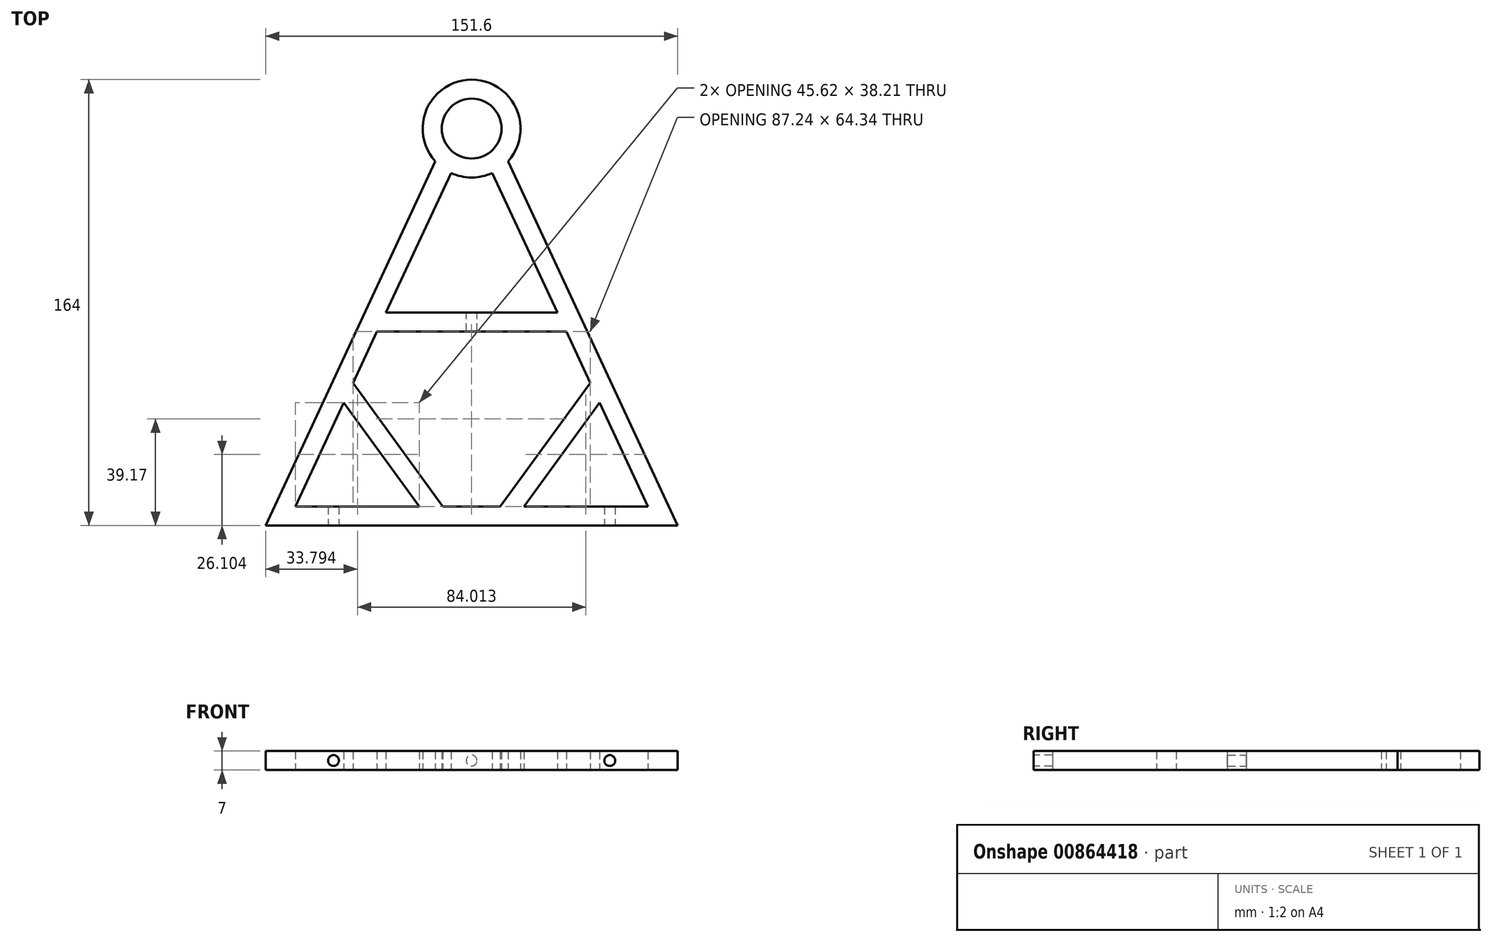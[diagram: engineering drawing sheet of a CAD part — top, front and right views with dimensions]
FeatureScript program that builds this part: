
annotation { "Feature Type Name" : "Feature", "Feature Type Description" : "" }
export const myFeature = defineFeature(function(context is Context, id is Id, definition is map)
    precondition{}
    {
        {
            var Q0;
            Q0=qCreatedBy(makeId("Top.planeOp"),FACE);
            var sketch = newSketch(context, id + "F0", { "sketchPlane" : qUnion([Q0])});
            skCircle(sketch, "E0", {"center": v(0, 0) * mm, "radius": 100 * mm, "construction": true});
            skCircle(sketch, "E1", {"center": v(0, 0) * mm, "radius": 25 * mm, "construction": true});
            skLineSegment(sketch, "E2", {"start": v(0, 0) * mm, "end": v(0, -152.48) * mm, "construction": true});
            skLineSegment(sketch, "E3", {"start": v(0, 0) * mm, "end": v(64.82, -139) * mm});
            skLineSegment(sketch, "E4", {"start": v(0, 0) * mm, "end": v(-64.82, -139) * mm});
            skCircle(sketch, "E5", {"center": v(0, 0) * mm, "radius": 11 * mm});
            skLineSegment(sketch, "E6.0", {"start": v(-6.34, 2.96) * mm, "end": v(-75.8, -146) * mm});
            skLineSegment(sketch, "E7.0", {"start": v(6.34, 2.96) * mm, "end": v(75.8, -146) * mm});
            skCircle(sketch, "E8.0", {"center": v(0, 0) * mm, "radius": 18 * mm});
            skLineSegment(sketch, "E9", {"start": v(57.36, -74.66) * mm, "end": v(0, -153.48) * mm});
            skLineSegment(sketch, "E10", {"start": v(0, -153.48) * mm, "end": v(-57.36, -74.66) * mm});
            skLineSegment(sketch, "E11", {"start": v(-57.36, -74.66) * mm, "end": v(57.36, -74.66) * mm});
            skLineSegment(sketch, "E12.0", {"start": v(71.1, -67.66) * mm, "end": v(0, -165.38) * mm});
            skLineSegment(sketch, "E12.1", {"start": v(-71.1, -67.66) * mm, "end": v(71.1, -67.66) * mm});
            skLineSegment(sketch, "E12.2", {"start": v(0, -165.38) * mm, "end": v(-71.1, -67.66) * mm});
            skLineSegment(sketch, "E13", {"start": v(-75.8, -146) * mm, "end": v(75.8, -146) * mm});
            skLineSegment(sketch, "E14.trimOffspring", {"start": v(-64.82, -139) * mm, "end": v(64.82, -139) * mm});
            skSolve(sketch);
        }
        {
            var Q0;
            {var subQ0=sQuery(id+"F0.wireOp",EDGE,"rMP4F2J8-MFNj-B9O5-1YN4-RzQH2zEwrkU1");Q0=makeQuery(id+"F0.imprint","IMPRINT",FACE,{"disambiguationData":[TD([[makeQuery(id+"F0.imprint","IMPRINT",EDGE,{"derivedFrom":subQ0}),-1.0]])]});}
            var Q1;
            {var subQ0=sQuery(id+"F0.wireOp",EDGE,"E10");Q1=makeQuery(id+"F0.imprint","IMPRINT",FACE,{"disambiguationData":[TD([[makeQuery(id+"F0.imprint","IMPRINT",EDGE,{"derivedFrom":subQ0}),1.0]])]});}
            var Q2;
            {var subQ0=sQuery(id+"F0.wireOp",EDGE,"E11");Q2=makeQuery(id+"F0.imprint","IMPRINT",FACE,{"disambiguationData":[TD([[makeQuery(id+"F0.imprint","IMPRINT",EDGE,{"derivedFrom":subQ0}),1.0]])]});}
            var Q3;
            {var subQ0=sQuery(id+"F0.wireOp",EDGE,"E9");Q3=makeQuery(id+"F0.imprint","IMPRINT",FACE,{"disambiguationData":[TD([[makeQuery(id+"F0.imprint","IMPRINT",EDGE,{"derivedFrom":subQ0}),1.0]])]});}
            var Q4;
            {var subQ8=sQuery(id+"F0.wireOp",EDGE,"1jrSBUuX-ILp1-f5az-bRsI-Kc6tBy7hKFYi");Q4=makeQuery(id+"F0.imprint","IMPRINT",FACE,{"disambiguationData":[TD([[makeQuery(id+"F0.imprint","IMPRINT",EDGE,{"derivedFrom":subQ8}),1.0]])]});}
            var Q5;
            {var subQ1=sQuery(id+"F0.wireOp",EDGE,"0f01eb31-d20b-408a-a949-16b7b9c288b3.0");var subQ5=sQuery(id+"F0.wireOp",EDGE,"E12.2");var subQ6=makeQuery(id+"F0.imprint","INTERSECT",VERTEX,{"derivedFrom":[subQ1,subQ5]});Q5=makeQuery(id+"F0.imprint","IMPRINT",FACE,{"disambiguationData":[TD([[makeQuery(id+"F0.imprint","IMPRINT",EDGE,{"disambiguationData":[TD([[subQ6,-1.0]])],"derivedFrom":subQ1}),1.0]])]});}
            var Q6;
            {var subQ1=sQuery(id+"F0.wireOp",EDGE,"E7.0");var subQ5=sQuery(id+"F0.wireOp",EDGE,"E12.1");var subQ6=makeQuery(id+"F0.imprint","INTERSECT",VERTEX,{"derivedFrom":[subQ1,subQ5]});Q6=makeQuery(id+"F0.imprint","IMPRINT",FACE,{"disambiguationData":[TD([[makeQuery(id+"F0.imprint","IMPRINT",EDGE,{"disambiguationData":[TD([[subQ6,-1.0]])],"derivedFrom":subQ1}),-1.0]])]});}
            var Q7;
            {var subQ0=sQuery(id+"F0.wireOp",EDGE,"E8.0");var subQ1=sQuery(id+"F0.wireOp",EDGE,"E3");var subQ2=makeQuery(id+"F0.imprint","INTERSECT",VERTEX,{"derivedFrom":[subQ1,subQ0]});Q7=makeQuery(id+"F0.imprint","IMPRINT",FACE,{"disambiguationData":[TD([[makeQuery(id+"F0.imprint","IMPRINT",EDGE,{"disambiguationData":[TD([[subQ2,-1.0]])],"derivedFrom":subQ1}),1.0]])]});}
            var Q8;
            {var subQ0=sQuery(id+"F0.wireOp",EDGE,"E12.1");var subQ1=sQuery(id+"F0.wireOp",EDGE,"E6.0");var subQ2=makeQuery(id+"F0.imprint","INTERSECT",VERTEX,{"derivedFrom":[subQ1,subQ0]});Q8=makeQuery(id+"F0.imprint","IMPRINT",FACE,{"disambiguationData":[TD([[makeQuery(id+"F0.imprint","IMPRINT",EDGE,{"disambiguationData":[TD([[subQ2,-1.0]])],"derivedFrom":subQ1}),1.0]])]});}
            var Q9;
            {var subQ0=sQuery(id+"F0.wireOp",EDGE,"E8.0");var subQ1=sQuery(id+"F0.wireOp",EDGE,"E4");var subQ2=makeQuery(id+"F0.imprint","INTERSECT",VERTEX,{"derivedFrom":[subQ1,subQ0]});Q9=makeQuery(id+"F0.imprint","IMPRINT",FACE,{"disambiguationData":[TD([[makeQuery(id+"F0.imprint","IMPRINT",EDGE,{"disambiguationData":[TD([[subQ2,-1.0]])],"derivedFrom":subQ1}),-1.0]])]});}
            var Q10;
            {var subQ0=sQuery(id+"F0.wireOp",EDGE,"E6.0");var subQ1=sQuery(id+"F0.wireOp",EDGE,"E5");var subQ2=makeQuery(id+"F0.imprint","INTERSECT",VERTEX,{"derivedFrom":[subQ1,subQ0]});Q10=makeQuery(id+"F0.imprint","IMPRINT",FACE,{"disambiguationData":[TD([[makeQuery(id+"F0.imprint","IMPRINT",EDGE,{"disambiguationData":[TD([[subQ2,1.0]])],"derivedFrom":subQ1}),-1.0]])]});}
            var Q11;
            {var subQ0=sQuery(id+"F0.wireOp",EDGE,"E5");var subQ1=sQuery(id+"F0.wireOp",EDGE,"E4");var subQ2=makeQuery(id+"F0.imprint","INTERSECT",VERTEX,{"derivedFrom":[subQ1,subQ0]});Q11=makeQuery(id+"F0.imprint","IMPRINT",FACE,{"disambiguationData":[TD([[makeQuery(id+"F0.imprint","IMPRINT",EDGE,{"disambiguationData":[TD([[subQ2,-1.0]])],"derivedFrom":subQ1}),-1.0]])]});}
            var Q12;
            {var subQ0=sQuery(id+"F0.wireOp",EDGE,"E5");var subQ1=sQuery(id+"F0.wireOp",EDGE,"E3");var subQ2=makeQuery(id+"F0.imprint","INTERSECT",VERTEX,{"derivedFrom":[subQ1,subQ0]});Q12=makeQuery(id+"F0.imprint","IMPRINT",FACE,{"disambiguationData":[TD([[makeQuery(id+"F0.imprint","IMPRINT",EDGE,{"disambiguationData":[TD([[subQ2,-1.0]])],"derivedFrom":subQ1}),-1.0]])]});}
            var Q13;
            {var subQ0=sQuery(id+"F0.wireOp",EDGE,"E5");var subQ1=sQuery(id+"F0.wireOp",EDGE,"E3");var subQ2=makeQuery(id+"F0.imprint","INTERSECT",VERTEX,{"derivedFrom":[subQ1,subQ0]});Q13=makeQuery(id+"F0.imprint","IMPRINT",FACE,{"disambiguationData":[TD([[makeQuery(id+"F0.imprint","IMPRINT",EDGE,{"disambiguationData":[TD([[subQ2,-1.0]])],"derivedFrom":subQ1}),1.0]])]});}
            var Q14;
            {var subQ0=sQuery(id+"F0.wireOp",EDGE,"E11");var subQ1=sQuery(id+"F0.wireOp",EDGE,"E3");var subQ2=makeQuery(id+"F0.imprint","INTERSECT",VERTEX,{"derivedFrom":[subQ1,subQ0]});Q14=makeQuery(id+"F0.imprint","IMPRINT",FACE,{"disambiguationData":[TD([[makeQuery(id+"F0.imprint","IMPRINT",EDGE,{"disambiguationData":[TD([[subQ2,-1.0]])],"derivedFrom":subQ1}),1.0]])]});}
            var Q15;
            {var subQ0=sQuery(id+"F0.wireOp",EDGE,"E11");var subQ1=sQuery(id+"F0.wireOp",EDGE,"E4");var subQ2=makeQuery(id+"F0.imprint","INTERSECT",VERTEX,{"derivedFrom":[subQ1,subQ0]});Q15=makeQuery(id+"F0.imprint","IMPRINT",FACE,{"disambiguationData":[TD([[makeQuery(id+"F0.imprint","IMPRINT",EDGE,{"disambiguationData":[TD([[subQ2,-1.0]])],"derivedFrom":subQ1}),-1.0]])]});}
            var Q16;
            {var subQ3=sQuery(id+"F0.wireOp",EDGE,"E4");var subQ7=sQuery(id+"F0.wireOp",EDGE,"E14.trimOffspring");var subQ10=makeQuery(id+"F0.imprint","INTERSECT",VERTEX,{"derivedFrom":[subQ3,subQ7]});Q16=makeQuery(id+"F0.imprint","IMPRINT",FACE,{"disambiguationData":[TD([[makeQuery(id+"F0.imprint","IMPRINT",EDGE,{"disambiguationData":[TD([[subQ10,1.0]])],"derivedFrom":subQ3}),-1.0]])]});}
            var Q17;
            {var subQ3=sQuery(id+"F0.wireOp",EDGE,"E14.trimOffspring");var subQ7=sQuery(id+"F0.wireOp",EDGE,"E3");var subQ9=makeQuery(id+"F0.imprint","INTERSECT",VERTEX,{"derivedFrom":[subQ7,subQ3]});Q17=makeQuery(id+"F0.imprint","IMPRINT",FACE,{"disambiguationData":[TD([[makeQuery(id+"F0.imprint","IMPRINT",EDGE,{"disambiguationData":[TD([[subQ9,1.0]])],"derivedFrom":subQ7}),1.0]])]});}
            var Q18;
            {var subQ0=sQuery(id+"F0.wireOp",EDGE,"E14.trimOffspring");var subQ1=sQuery(id+"F0.wireOp",EDGE,"E9");var subQ2=makeQuery(id+"F0.imprint","INTERSECT",VERTEX,{"derivedFrom":[subQ1,subQ0]});Q18=makeQuery(id+"F0.imprint","IMPRINT",FACE,{"disambiguationData":[TD([[makeQuery(id+"F0.imprint","IMPRINT",EDGE,{"disambiguationData":[TD([[subQ2,-1.0]])],"derivedFrom":subQ1}),-1.0]])]});}
            extrude(context, id + "F1", {"entities" : qUnion([Q0, Q1, Q2, Q3, Q4, Q5, Q6, Q7, Q8, Q9, Q10, Q11, Q12, Q13, Q14, Q15, Q16, Q17, Q18]), "depth" : 7 * mm, "offsetDistance" : 25 * mm});
        }
        {
            var Q0;
            Q0=makeQuery(id+"F1.opExtrude","SWEPT_FACE",FACE,{"disambiguationData":[OSD([sQuery(id+"F0.wireOp",EDGE,"E12.1")])]});
            var sketch = newSketch(context, id + "F2", { "sketchPlane" : qUnion([Q0])});
            skCircle(sketch, "E15", {"center": v(0, 3.5) * mm, "radius": 2 * mm});
            skSolve(sketch);
        }
        {
            var Q0;
            Q0=makeQuery(id+"F2.imprint","IMPRINT",FACE,{"disambiguationData":[TD([[makeQuery(id+"F2.imprint","IMPRINT",EDGE,{"derivedFrom":sQuery(id+"F2.wireOp",EDGE,"E15")}),1.0]])]});
            extrude(context, id + "F3", {"entities" : qUnion([Q0]), "operationType" : NewBodyOperationType.REMOVE, "oppositeDirection" : true, "depth" : 8 * mm, "offsetDistance" : 25 * mm});
        }
        {
            var Q0;
            Q0=makeQuery(id+"F1.opExtrude","SWEPT_FACE",FACE,{"disambiguationData":[OSD([sQuery(id+"F0.wireOp",EDGE,"E13")])]});
            var sketch = newSketch(context, id + "F4", { "sketchPlane" : qUnion([Q0])});
            skCircle(sketch, "E16", {"center": v(-50.8, 3.5) * mm, "radius": 2 * mm});
            skLineSegment(sketch, "E17", {"start": v(-75.8, 3.5) * mm, "end": v(-50.8, 3.5) * mm, "construction": true});
            skLineSegment(sketch, "E18", {"start": v(75.8, 3.5) * mm, "end": v(50.8, 3.5) * mm, "construction": true});
            skCircle(sketch, "E19", {"center": v(50.8, 3.5) * mm, "radius": 2 * mm});
            skSolve(sketch);
        }
        {
            var Q0;
            Q0=makeQuery(id+"F4.imprint","IMPRINT",FACE,{"disambiguationData":[TD([[makeQuery(id+"F4.imprint","IMPRINT",EDGE,{"derivedFrom":sQuery(id+"F4.wireOp",EDGE,"E16")}),1.0]])]});
            var Q1;
            Q1=makeQuery(id+"F4.imprint","IMPRINT",FACE,{"disambiguationData":[TD([[makeQuery(id+"F4.imprint","IMPRINT",EDGE,{"derivedFrom":sQuery(id+"F4.wireOp",EDGE,"E19")}),1.0]])]});
            extrude(context, id + "F5", {"entities" : qUnion([Q0, Q1]), "operationType" : NewBodyOperationType.REMOVE, "oppositeDirection" : true, "depth" : 8 * mm, "offsetDistance" : 25 * mm});
        }
    });
